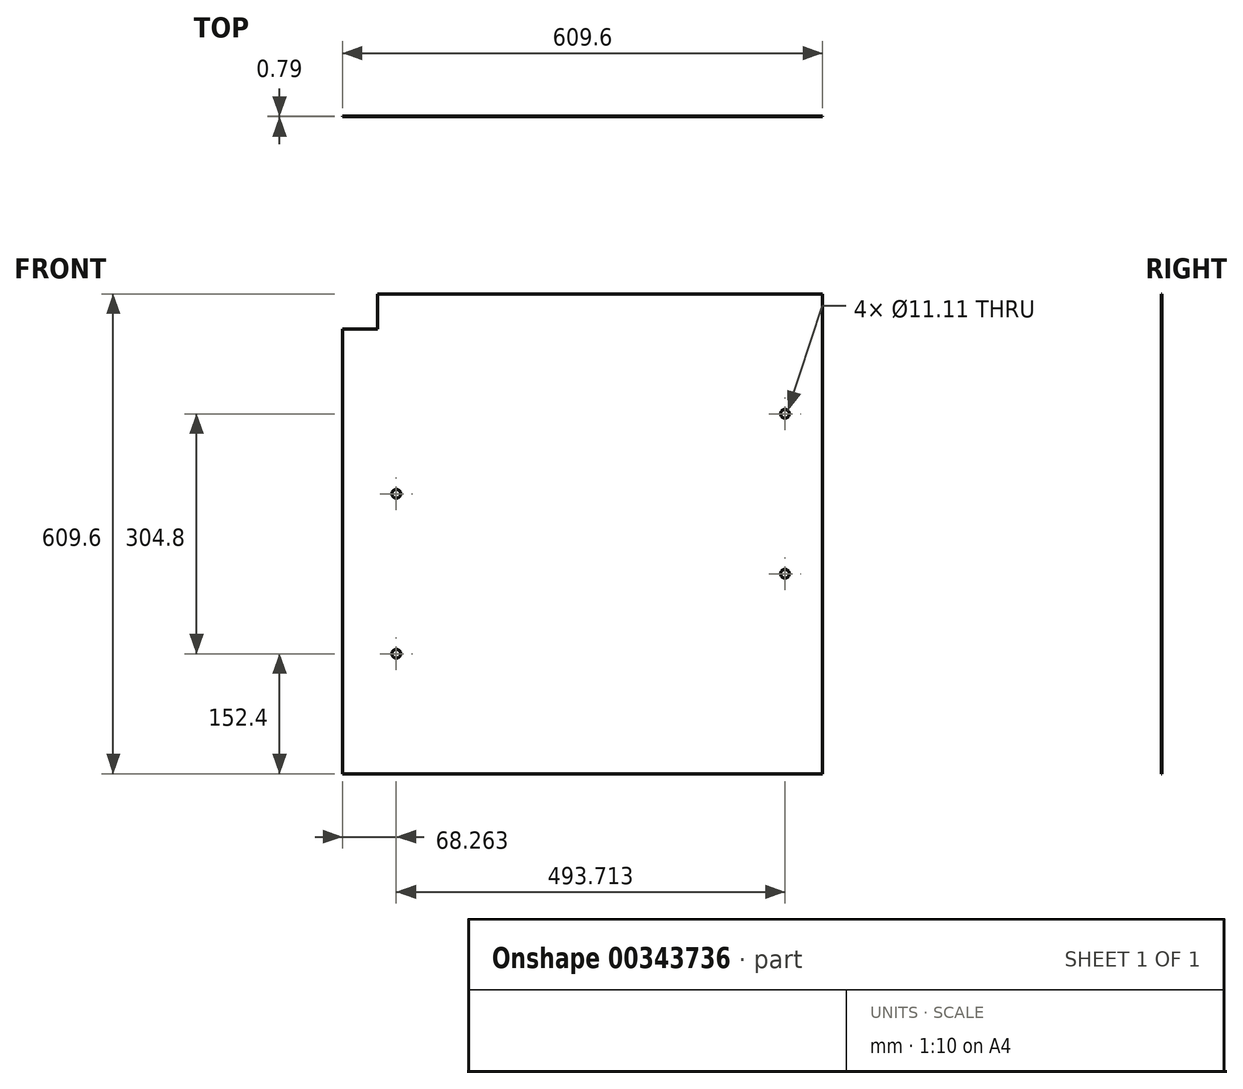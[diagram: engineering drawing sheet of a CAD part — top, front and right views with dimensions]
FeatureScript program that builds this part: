
annotation { "Feature Type Name" : "Feature", "Feature Type Description" : "" }
export const myFeature = defineFeature(function(context is Context, id is Id, definition is map)
    precondition{}
    {
        {
            var Q0;
            Q0=qCreatedBy(makeId("Front.planeOp"),FACE);
            var sketch = newSketch(context, id + "F0", { "sketchPlane" : qUnion([Q0])});
            skLineSegment(sketch, "E0.bottom", {"start": v(0, 0) * mm, "end": v(609.6, 0) * mm});
            skLineSegment(sketch, "E0.top", {"start": v(0, 609.6) * mm, "end": v(609.6, 609.6) * mm});
            skLineSegment(sketch, "E0.left", {"start": v(0, 0) * mm, "end": v(0, 609.6) * mm});
            skLineSegment(sketch, "E0.right", {"start": v(609.6, 0) * mm, "end": v(609.6, 609.6) * mm});
            skLineSegment(sketch, "E1.bottom", {"start": v(0, 609.6) * mm, "end": v(44.45, 609.6) * mm});
            skLineSegment(sketch, "E1.top", {"start": v(0, 565.15) * mm, "end": v(44.45, 565.15) * mm});
            skLineSegment(sketch, "E1.left", {"start": v(0, 609.6) * mm, "end": v(0, 565.15) * mm});
            skLineSegment(sketch, "E1.right", {"start": v(44.45, 609.6) * mm, "end": v(44.45, 565.15) * mm});
            skSolve(sketch);
        }
        {
            var Q0;
            Q0=makeQuery(id+"F0.imprint","IMPRINT",FACE,{"disambiguationData":[TD([[makeQuery(id+"F0.imprint","IMPRINT",EDGE,{"derivedFrom":sQuery(id+"F0.wireOp",EDGE,"E0.bottom")}),1.0]])]});
            extrude(context, id + "F1", {"entities" : qUnion([Q0]), "depth" : 0.8 * mm});
        }
        {
            var Q0;
            Q0=makeQuery(id+"F1.opExtrude","CAP_FACE",FACE,{"disambiguationData":[OSD([sQuery(id+"F0.wireOp",EDGE,"E0.bottom"),sQuery(id+"F0.wireOp",EDGE,"E0.top"),sQuery(id+"F0.wireOp",EDGE,"E0.left"),sQuery(id+"F0.wireOp",EDGE,"E0.right"),sQuery(id+"F0.wireOp",EDGE,"lgMoYjj3-GGwG-qvfQ-sMHt-zzlWqoId0sSI.top"),sQuery(id+"F0.wireOp",EDGE,"lgMoYjj3-GGwG-qvfQ-sMHt-zzlWqoId0sSI.right")])],"isStart":false});
            var sketch = newSketch(context, id + "F2", { "sketchPlane" : qUnion([Q0])});
            skCircle(sketch, "E2", {"center": v(68.26, 152.4) * mm, "radius": 5.56 * mm});
            skCircle(sketch, "E3", {"center": v(68.26, 355.6) * mm, "radius": 5.56 * mm});
            skCircle(sketch, "E4", {"center": v(561.98, 457.2) * mm, "radius": 5.56 * mm});
            skCircle(sketch, "E5", {"center": v(561.98, 254) * mm, "radius": 5.56 * mm});
            skSolve(sketch);
        }
        {
            var Q0;
            Q0=makeQuery(id+"F2.imprint","IMPRINT",FACE,{"disambiguationData":[TD([[makeQuery(id+"F2.imprint","IMPRINT",EDGE,{"derivedFrom":sQuery(id+"F2.wireOp",EDGE,"E5")}),1.0]])]});
            var Q1;
            Q1=makeQuery(id+"F2.imprint","IMPRINT",FACE,{"disambiguationData":[TD([[makeQuery(id+"F2.imprint","IMPRINT",EDGE,{"derivedFrom":sQuery(id+"F2.wireOp",EDGE,"E4")}),1.0]])]});
            var Q2;
            Q2=makeQuery(id+"F2.imprint","IMPRINT",FACE,{"disambiguationData":[TD([[makeQuery(id+"F2.imprint","IMPRINT",EDGE,{"derivedFrom":sQuery(id+"F2.wireOp",EDGE,"E2")}),1.0]])]});
            var Q3;
            Q3=makeQuery(id+"F2.imprint","IMPRINT",FACE,{"disambiguationData":[TD([[makeQuery(id+"F2.imprint","IMPRINT",EDGE,{"derivedFrom":sQuery(id+"F2.wireOp",EDGE,"E3")}),1.0]])]});
            extrude(context, id + "F3", {"entities" : qUnion([Q0, Q1, Q2, Q3]), "operationType" : NewBodyOperationType.REMOVE, "oppositeDirection" : true, "depth" : 25.4 * mm});
        }
    });
